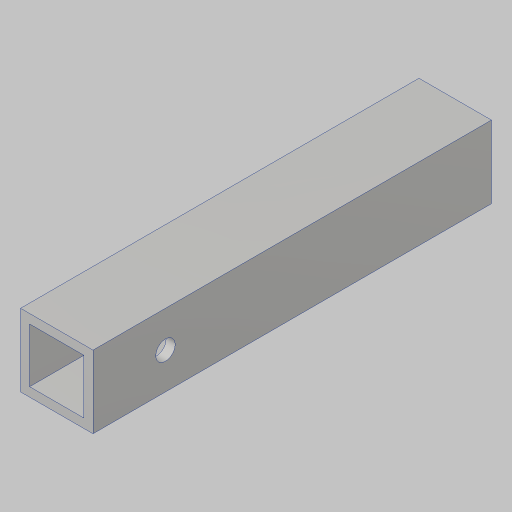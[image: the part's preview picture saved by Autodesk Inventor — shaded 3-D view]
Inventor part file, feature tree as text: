
AUTODESK INVENTOR PART (.ipt)
format: ipt  version: 2023.5 (Build 275446000, 446)  size: 107,008 bytes
history: native  units: in
note: dims shown in document units (in); Inventor stores cm internally (conversion verified against a paired STEP export)
features: extrude x1, hole x1, sketch x1
ambient origin geometry x8: Origin, YZ Plane, XZ Plane, XY Plane, X Axis, Y Axis, Z Axis, Center Point
bodies: Solid1 (feature_tree)
feature tree (3):
  extrude  "Extrusion1"  Depth=1.0in
  hole  "Hole1"  [1 undecoded]
  sketch  "Sketch2"  dims[d4=0.0in d5=1.0in d6=0.266in d7=0.75in d8=0.507in d9=0.25in d10=0.5635in d11=1.0in d12=0.8108in]
note: 1 required parameter value undecoded (feature->parameter linkage not recoverable at this tier; creation-order binding heuristic only, values carry confidence <= 0.55)
